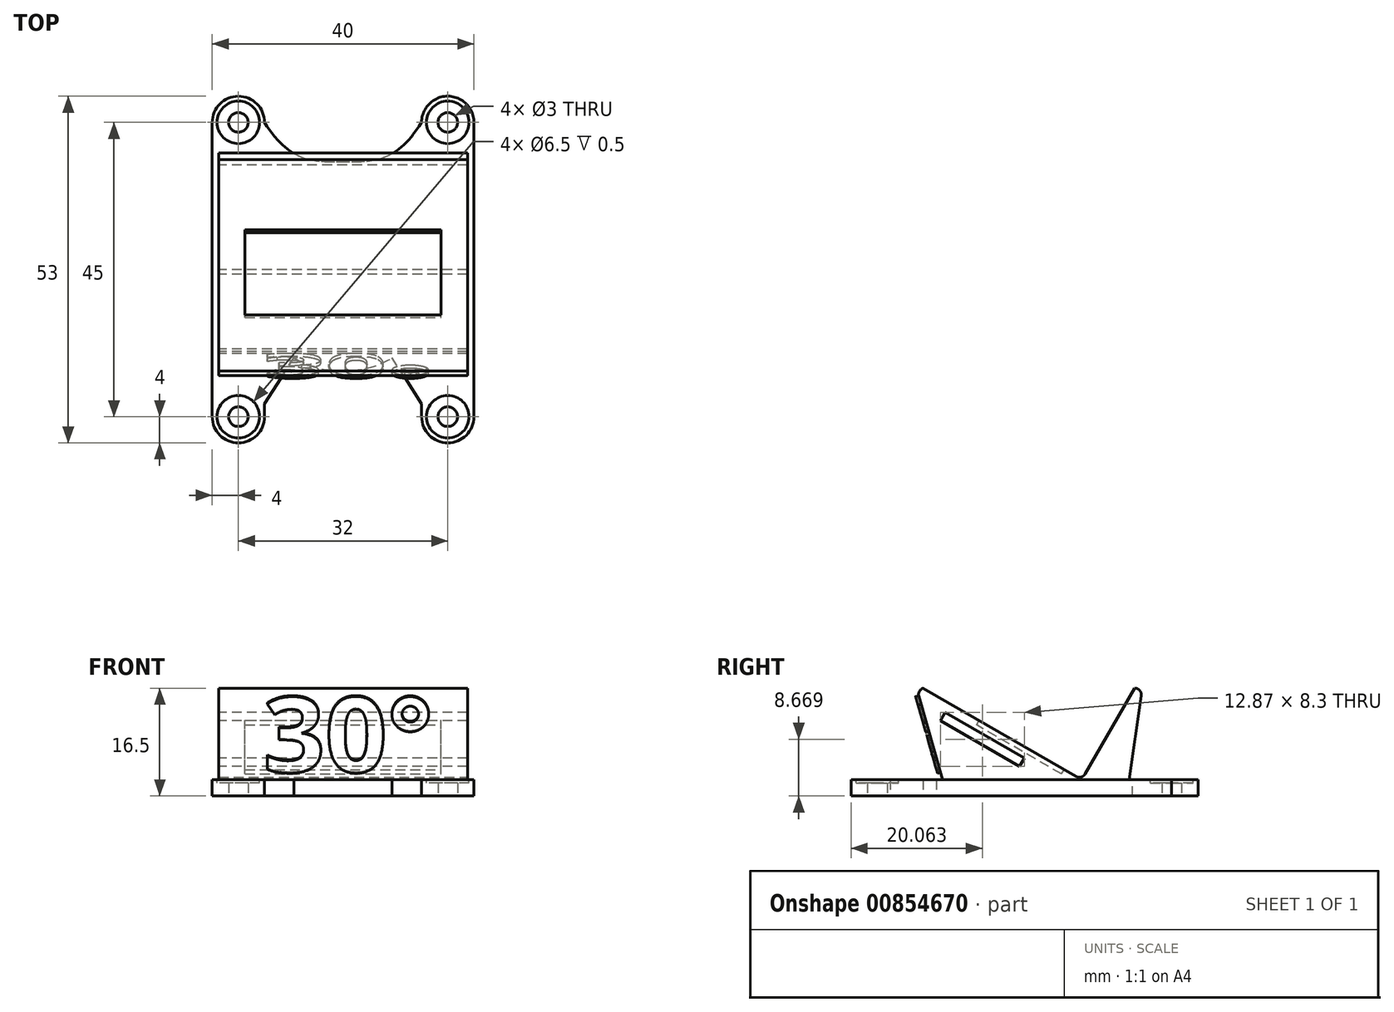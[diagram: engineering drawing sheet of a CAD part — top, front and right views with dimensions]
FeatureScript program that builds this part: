
annotation { "Feature Type Name" : "Feature", "Feature Type Description" : "" }
export const myFeature = defineFeature(function(context is Context, id is Id, definition is map)
    precondition{}
    {
        {
            var Q0;
            Q0=qCreatedBy(makeId("Top.planeOp"),FACE);
            var sketch = newSketch(context, id + "F0", { "sketchPlane" : qUnion([Q0])});
            skCircle(sketch, "E0", {"center": v(-16, 22.5) * mm, "radius": 4 * mm});
            skCircle(sketch, "E1", {"center": v(16, 22.5) * mm, "radius": 4 * mm});
            skCircle(sketch, "E2", {"center": v(-16, -22.5) * mm, "radius": 4 * mm});
            skCircle(sketch, "E3", {"center": v(16, -22.5) * mm, "radius": 4 * mm});
            skLineSegment(sketch, "E4", {"start": v(-20, 22.5) * mm, "end": v(-20, -22.5) * mm});
            skLineSegment(sketch, "E5", {"start": v(20, 22.55) * mm, "end": v(20, -22.5) * mm});
            skLineSegment(sketch, "E6", {"start": v(-12, -22.5) * mm, "end": v(-12, -20.5) * mm});
            skLineSegment(sketch, "E7", {"start": v(12, -22.5) * mm, "end": v(12, -20.5) * mm});
            skLineSegment(sketch, "E8", {"start": v(-12, -20.5) * mm, "end": v(-7.5, -13.5) * mm});
            skLineSegment(sketch, "E9", {"start": v(12, -20.5) * mm, "end": v(7.5, -13.5) * mm});
            skFitSpline(sketch, "E10", {"points": [v(-7.5, -13.5) * mm, v(0, -15.5) * mm, v(7.5, -13.5) * mm], "startDerivative": vector(15, -9) * mm, "endDerivative": vector(15, 9) * mm});
            skFitSpline(sketch, "E11", {"points": [v(-12, 22.5) * mm, v(0, 16.5) * mm, v(12, 22.5) * mm], "startDerivative": vector(24, -39) * mm, "endDerivative": vector(24, 39) * mm});
            skSolve(sketch);
        }
        {
            var Q0;
            Q0=qSketchRegion(id+"F0",true);
            extrude(context, id + "F1", {"entities" : qUnion([Q0]), "depth" : 2.5 * mm, "offsetDistance" : 25 * mm});
        }
        {
            var Q0;
            Q0=qCreatedBy(makeId("Right.planeOp"),FACE);
            var sketch = newSketch(context, id + "F2", { "sketchPlane" : qUnion([Q0])});
            skLineSegment(sketch, "E12", {"start": v(16, 2.5) * mm, "end": v(-12.5, 2.5) * mm});
            skLineSegment(sketch, "E13", {"start": v(-12.5, 2.5) * mm, "end": v(-16.5, 16.5) * mm});
            skLineSegment(sketch, "E14", {"start": v(-16.5, 16.5) * mm, "end": v(18, 16.5) * mm});
            skLineSegment(sketch, "E15", {"start": v(18, 16.5) * mm, "end": v(16, 2.5) * mm});
            skSolve(sketch);
        }
        {
            var Q0;
            Q0=qSketchRegion(id+"F2",true);
            extrude(context, id + "F3", {"entities" : qUnion([Q0]), "endBound" : BoundingType.SYMMETRIC, "depth" : 38 * mm, "offsetDistance" : 25 * mm});
        }
        {
            var Q0;
            Q0=makeQuery(id+"F3.opExtrude","CAP_FACE",FACE,{"disambiguationData":[OSD([sQuery(id+"F2.wireOp",EDGE,"YzHD2A4w-FKaB-bjk7-Ghrs-dXmW5guKQ4VY"),sQuery(id+"F2.wireOp",EDGE,"E12"),sQuery(id+"F2.wireOp",EDGE,"E13"),sQuery(id+"F2.wireOp",EDGE,"E14"),sQuery(id+"F2.wireOp",EDGE,"zXvGVPE5-xHOz-sBgs-eNty-2IJ9yV3vvyon")])],"isStart":true});
            var sketch = newSketch(context, id + "F4", { "sketchPlane" : qUnion([Q0])});
            skLineSegment(sketch, "E16", {"start": v(-16.83, 16.5) * mm, "end": v(-8.75, 2.5) * mm});
            skLineSegment(sketch, "E17", {"start": v(-8.75, 2.5) * mm, "end": v(15.5, 16.5) * mm});
            skLineSegment(sketch, "E18", {"start": v(15.5, 16.5) * mm, "end": v(-16.83, 16.5) * mm});
            skSolve(sketch);
        }
        {
            var Q0;
            Q0=qSketchRegion(id+"F4",true);
            extrude(context, id + "F5", {"entities" : qUnion([Q0]), "oppositeDirection" : true, "depth" : 40 * mm, "offsetDistance" : 25 * mm});
        }
        {
            var Q0;
            Q0=makeQuery(id+"F5.opExtrude","SWEPT_BODY",BODY,{"disambiguationData":[OSD([sQuery(id+"F4.wireOp",EDGE,"E16"),sQuery(id+"F4.wireOp",EDGE,"E17"),sQuery(id+"F4.wireOp",EDGE,"E18")])]});
            var Q1;
            Q1=makeQuery(id+"F3.opExtrude","SWEPT_BODY",BODY,{"disambiguationData":[OSD([sQuery(id+"F2.wireOp",EDGE,"YzHD2A4w-FKaB-bjk7-Ghrs-dXmW5guKQ4VY"),sQuery(id+"F2.wireOp",EDGE,"E12"),sQuery(id+"F2.wireOp",EDGE,"E13"),sQuery(id+"F2.wireOp",EDGE,"E14"),sQuery(id+"F2.wireOp",EDGE,"zXvGVPE5-xHOz-sBgs-eNty-2IJ9yV3vvyon")])]});
            booleanBodies(context, id + "F6", {"operationType" : BooleanOperationType.SUBTRACTION, "tools" : qUnion([Q0]), "targets" : qUnion([Q1])});
        }
        {
            var Q0;
            Q0=sQuery(id+"F0.wireOp",VERTEX,"E0.center");
            var Q1;
            Q1=sQuery(id+"F0.wireOp",VERTEX,"E1.center");
            var Q2;
            Q2=sQuery(id+"F0.wireOp",VERTEX,"E2.center");
            var Q3;
            Q3=sQuery(id+"F0.wireOp",VERTEX,"E3.center");
            var Q4;
            Q4=makeQuery(id+"F1.opExtrude","SWEPT_BODY",BODY,{"disambiguationData":[OSD([sQuery(id+"F0.wireOp",EDGE,"E0"),sQuery(id+"F0.wireOp",EDGE,"E1"),sQuery(id+"F0.wireOp",EDGE,"E2"),sQuery(id+"F0.wireOp",EDGE,"E3"),sQuery(id+"F0.wireOp",EDGE,"E4"),sQuery(id+"F0.wireOp",EDGE,"E5"),sQuery(id+"F0.wireOp",EDGE,"E6"),sQuery(id+"F0.wireOp",EDGE,"E7"),sQuery(id+"F0.wireOp",EDGE,"E8"),sQuery(id+"F0.wireOp",EDGE,"E9"),sQuery(id+"F0.wireOp",EDGE,"E10"),sQuery(id+"F0.wireOp",EDGE,"E11")])]});
            hole(context, id + "F7", {"style" : HoleStyle.SIMPLE, "endStyle" : HoleEndStyle.THROUGH, "oppositeDirection" : true, "holeDiameter" : 3 * mm, "tappedDepth" : 12 * mm, "tapClearance" : 3, "locations" : qUnion([Q0, Q1, Q2, Q3]), "scope" : qUnion([Q4])});
        }
        {
            var Q0;
            Q0=makeQuery(id+"F1.opExtrude","CAP_FACE",FACE,{"disambiguationData":[OSD([sQuery(id+"F0.wireOp",EDGE,"E0"),sQuery(id+"F0.wireOp",EDGE,"E1"),sQuery(id+"F0.wireOp",EDGE,"E2"),sQuery(id+"F0.wireOp",EDGE,"E3"),sQuery(id+"F0.wireOp",EDGE,"E4"),sQuery(id+"F0.wireOp",EDGE,"E5"),sQuery(id+"F0.wireOp",EDGE,"E6"),sQuery(id+"F0.wireOp",EDGE,"E7"),sQuery(id+"F0.wireOp",EDGE,"E8"),sQuery(id+"F0.wireOp",EDGE,"E9"),sQuery(id+"F0.wireOp",EDGE,"E10"),sQuery(id+"F0.wireOp",EDGE,"E11")])],"isStart":false});
            var sketch = newSketch(context, id + "F8", { "sketchPlane" : qUnion([Q0])});
            skCircle(sketch, "E19", {"center": v(-16, 22.5) * mm, "radius": 3.25 * mm});
            skCircle(sketch, "E20", {"center": v(16, 22.5) * mm, "radius": 3.25 * mm});
            skCircle(sketch, "E21", {"center": v(-16, -22.5) * mm, "radius": 3.25 * mm});
            skCircle(sketch, "E22", {"center": v(16, -22.5) * mm, "radius": 3.25 * mm});
            skSolve(sketch);
        }
        {
            var Q0;
            Q0=qSketchRegion(id+"F8",true);
            extrude(context, id + "F9", {"entities" : qUnion([Q0]), "oppositeDirection" : true, "depth" : 0.5 * mm, "offsetDistance" : 25 * mm});
        }
        {
            var Q0;
            Q0=makeQuery(id+"F9.opExtrude","SWEPT_BODY",BODY,{"disambiguationData":[OSD([sQuery(id+"F8.wireOp",EDGE,"E19")])]});
            var Q1;
            Q1=makeQuery(id+"F9.opExtrude","SWEPT_BODY",BODY,{"disambiguationData":[OSD([sQuery(id+"F8.wireOp",EDGE,"E20")])]});
            var Q2;
            Q2=makeQuery(id+"F9.opExtrude","SWEPT_BODY",BODY,{"disambiguationData":[OSD([sQuery(id+"F8.wireOp",EDGE,"E21")])]});
            var Q3;
            Q3=makeQuery(id+"F9.opExtrude","SWEPT_BODY",BODY,{"disambiguationData":[OSD([sQuery(id+"F8.wireOp",EDGE,"E22")])]});
            var Q4;
            Q4=makeQuery(id+"F1.opExtrude","SWEPT_BODY",BODY,{"disambiguationData":[OSD([sQuery(id+"F0.wireOp",EDGE,"E0"),sQuery(id+"F0.wireOp",EDGE,"E1"),sQuery(id+"F0.wireOp",EDGE,"E2"),sQuery(id+"F0.wireOp",EDGE,"E3"),sQuery(id+"F0.wireOp",EDGE,"E4"),sQuery(id+"F0.wireOp",EDGE,"E5"),sQuery(id+"F0.wireOp",EDGE,"E6"),sQuery(id+"F0.wireOp",EDGE,"E7"),sQuery(id+"F0.wireOp",EDGE,"E8"),sQuery(id+"F0.wireOp",EDGE,"E9"),sQuery(id+"F0.wireOp",EDGE,"E10"),sQuery(id+"F0.wireOp",EDGE,"E11")])]});
            booleanBodies(context, id + "F10", {"operationType" : BooleanOperationType.SUBTRACTION, "tools" : qUnion([Q0, Q1, Q2, Q3]), "targets" : qUnion([Q4])});
        }
        {
            var Q0;
            Q0=makeQuery(id+"F6.opBoolean","COPY",FACE,{"derivedFrom":makeQuery(id+"F5.opExtrude","SWEPT_FACE",FACE,{"disambiguationData":[OSD([sQuery(id+"F4.wireOp",EDGE,"E17")])]})});
            var sketch = newSketch(context, id + "F11", { "sketchPlane" : qUnion([Q0])});
            skLineSegment(sketch, "E23.bottom", {"start": v(-15, 3.22) * mm, "end": v(15, 3.22) * mm});
            skLineSegment(sketch, "E23.top", {"start": v(-15, -11.78) * mm, "end": v(15, -11.78) * mm});
            skLineSegment(sketch, "E23.left", {"start": v(-15, 3.22) * mm, "end": v(-15, -11.78) * mm});
            skLineSegment(sketch, "E23.right", {"start": v(15, 3.22) * mm, "end": v(15, -11.78) * mm});
            skSolve(sketch);
        }
        {
            var Q0;
            Q0=qSketchRegion(id+"F11",true);
            extrude(context, id + "F12", {"entities" : qUnion([Q0]), "oppositeDirection" : true, "depth" : 0.8 * mm, "offsetDistance" : 25 * mm});
        }
        {
            var Q0;
            Q0=makeQuery(id+"F12.opExtrude","SWEPT_BODY",BODY,{"disambiguationData":[OSD([sQuery(id+"F11.wireOp",EDGE,"E23.bottom"),sQuery(id+"F11.wireOp",EDGE,"E23.top"),sQuery(id+"F11.wireOp",EDGE,"E23.left"),sQuery(id+"F11.wireOp",EDGE,"E23.right")])]});
            var Q1;
            Q1=makeQuery(id+"F6.opBoolean","SPLIT",BODY,{"disambiguationData":[OD(1.0)],"derivedFrom":makeQuery(id+"F3.opExtrude","SWEPT_BODY",BODY,{"disambiguationData":[OSD([sQuery(id+"F2.wireOp",EDGE,"YzHD2A4w-FKaB-bjk7-Ghrs-dXmW5guKQ4VY"),sQuery(id+"F2.wireOp",EDGE,"E12"),sQuery(id+"F2.wireOp",EDGE,"E13"),sQuery(id+"F2.wireOp",EDGE,"E14"),sQuery(id+"F2.wireOp",EDGE,"zXvGVPE5-xHOz-sBgs-eNty-2IJ9yV3vvyon")])]})});
            var Q2;
            Q2=makeQuery(id+"F6.opBoolean","SPLIT",BODY,{"disambiguationData":[OD(0.0)],"derivedFrom":makeQuery(id+"F3.opExtrude","SWEPT_BODY",BODY,{"disambiguationData":[OSD([sQuery(id+"F2.wireOp",EDGE,"E12"),sQuery(id+"F2.wireOp",EDGE,"E13"),sQuery(id+"F2.wireOp",EDGE,"E14"),sQuery(id+"F2.wireOp",EDGE,"E15")])]})});
            booleanBodies(context, id + "F13", {"operationType" : BooleanOperationType.SUBTRACTION, "tools" : qUnion([Q0]), "targets" : qUnion([Q1, Q2])});
        }
        {
            var Q0;
            {var subQ0=sQuery(id+"F2.wireOp",EDGE,"E12");var subQ1=sQuery(id+"F2.wireOp",EDGE,"E13");Q0=makeQuery(id+"F6.opBoolean","SPLIT",FACE,{"disambiguationData":[TD([makeQuery(id+"F3.opExtrude","SWEPT_FACE",FACE,{"disambiguationData":[OSD([subQ1])]})])],"derivedFrom":makeQuery(id+"F3.opExtrude","CAP_FACE",FACE,{"disambiguationData":[OSD([sQuery(id+"F2.wireOp",EDGE,"YzHD2A4w-FKaB-bjk7-Ghrs-dXmW5guKQ4VY"),subQ0,subQ1,sQuery(id+"F2.wireOp",EDGE,"E14"),sQuery(id+"F2.wireOp",EDGE,"zXvGVPE5-xHOz-sBgs-eNty-2IJ9yV3vvyon")])],"isStart":true})});}
            var sketch = newSketch(context, id + "F14", { "sketchPlane" : qUnion([Q0])});
            skLineSegment(sketch, "E24", {"start": v(0, 5.82) * mm, "end": v(12.12, 12.82) * mm});
            skLineSegment(sketch, "E25", {"start": v(12.12, 12.82) * mm, "end": v(12.87, 11.52) * mm});
            skLineSegment(sketch, "E26", {"start": v(12.87, 11.52) * mm, "end": v(0.75, 4.52) * mm});
            skLineSegment(sketch, "E27", {"start": v(0.75, 4.52) * mm, "end": v(0, 5.82) * mm});
            skSolve(sketch);
        }
        {
            var Q0;
            Q0=qSketchRegion(id+"F14",true);
            extrude(context, id + "F15", {"entities" : qUnion([Q0]), "oppositeDirection" : true, "depth" : 40 * mm, "offsetDistance" : 25 * mm});
        }
        {
            var Q0;
            Q0=makeQuery(id+"F15.opExtrude","SWEPT_BODY",BODY,{"disambiguationData":[OSD([sQuery(id+"F14.wireOp",EDGE,"E24"),sQuery(id+"F14.wireOp",EDGE,"E25"),sQuery(id+"F14.wireOp",EDGE,"E26"),sQuery(id+"F14.wireOp",EDGE,"E27")])]});
            var Q1;
            Q1=makeQuery(id+"F6.opBoolean","SPLIT",BODY,{"disambiguationData":[OD(1.0)],"derivedFrom":makeQuery(id+"F3.opExtrude","SWEPT_BODY",BODY,{"disambiguationData":[OSD([sQuery(id+"F2.wireOp",EDGE,"YzHD2A4w-FKaB-bjk7-Ghrs-dXmW5guKQ4VY"),sQuery(id+"F2.wireOp",EDGE,"E12"),sQuery(id+"F2.wireOp",EDGE,"E13"),sQuery(id+"F2.wireOp",EDGE,"E14"),sQuery(id+"F2.wireOp",EDGE,"zXvGVPE5-xHOz-sBgs-eNty-2IJ9yV3vvyon")])]})});
            var Q2;
            Q2=makeQuery(id+"F6.opBoolean","SPLIT",BODY,{"disambiguationData":[OD(0.0)],"derivedFrom":makeQuery(id+"F3.opExtrude","SWEPT_BODY",BODY,{"disambiguationData":[OSD([sQuery(id+"F2.wireOp",EDGE,"E12"),sQuery(id+"F2.wireOp",EDGE,"E13"),sQuery(id+"F2.wireOp",EDGE,"E14"),sQuery(id+"F2.wireOp",EDGE,"E15")])]})});
            booleanBodies(context, id + "F16", {"operationType" : BooleanOperationType.SUBTRACTION, "tools" : qUnion([Q0]), "targets" : qUnion([Q1, Q2])});
        }
        {
            var Q0;
            Q0=makeQuery(id+"F1.opExtrude","SWEPT_BODY",BODY,{"disambiguationData":[OSD([sQuery(id+"F0.wireOp",EDGE,"E0"),sQuery(id+"F0.wireOp",EDGE,"E1"),sQuery(id+"F0.wireOp",EDGE,"E2"),sQuery(id+"F0.wireOp",EDGE,"E3"),sQuery(id+"F0.wireOp",EDGE,"E4"),sQuery(id+"F0.wireOp",EDGE,"E5"),sQuery(id+"F0.wireOp",EDGE,"E6"),sQuery(id+"F0.wireOp",EDGE,"E7"),sQuery(id+"F0.wireOp",EDGE,"E8"),sQuery(id+"F0.wireOp",EDGE,"E9"),sQuery(id+"F0.wireOp",EDGE,"E10"),sQuery(id+"F0.wireOp",EDGE,"E11")])]});
            var Q1;
            Q1=makeQuery(id+"F6.opBoolean","SPLIT",BODY,{"disambiguationData":[OD(0.0)],"derivedFrom":makeQuery(id+"F3.opExtrude","SWEPT_BODY",BODY,{"disambiguationData":[OSD([sQuery(id+"F2.wireOp",EDGE,"YzHD2A4w-FKaB-bjk7-Ghrs-dXmW5guKQ4VY"),sQuery(id+"F2.wireOp",EDGE,"E12"),sQuery(id+"F2.wireOp",EDGE,"E13"),sQuery(id+"F2.wireOp",EDGE,"E14"),sQuery(id+"F2.wireOp",EDGE,"zXvGVPE5-xHOz-sBgs-eNty-2IJ9yV3vvyon")])]})});
            var Q2;
            Q2=makeQuery(id+"F6.opBoolean","SPLIT",BODY,{"disambiguationData":[OD(1.0)],"derivedFrom":makeQuery(id+"F3.opExtrude","SWEPT_BODY",BODY,{"disambiguationData":[OSD([sQuery(id+"F2.wireOp",EDGE,"YzHD2A4w-FKaB-bjk7-Ghrs-dXmW5guKQ4VY"),sQuery(id+"F2.wireOp",EDGE,"E12"),sQuery(id+"F2.wireOp",EDGE,"E13"),sQuery(id+"F2.wireOp",EDGE,"E14"),sQuery(id+"F2.wireOp",EDGE,"zXvGVPE5-xHOz-sBgs-eNty-2IJ9yV3vvyon")])]})});
            booleanBodies(context, id + "F17", {"operationType" : BooleanOperationType.UNION, "tools" : qUnion([Q0, Q1, Q2])});
        }
        {
            var Q0;
            Q0=makeQuery(id+"F3.opExtrude","SWEPT_EDGE",EDGE,{"disambiguationData":[OSD([sQuery(id+"F2.wireOp",EDGE,"E12"),sQuery(id+"F2.wireOp",EDGE,"E13")])]});
            var Q1;
            Q1=makeQuery(id+"F3.opExtrude","SWEPT_EDGE",EDGE,{"disambiguationData":[OSD([sQuery(id+"F2.wireOp",EDGE,"E14"),sQuery(id+"F2.wireOp",EDGE,"zXvGVPE5-xHOz-sBgs-eNty-2IJ9yV3vvyon")])]});
            var Q2;
            {var subQ0=sQuery(id+"F2.wireOp",EDGE,"E12");var subQ2=sQuery(id+"F4.wireOp",EDGE,"E17");var subQ3=sQuery(id+"F4.wireOp",EDGE,"E16");var subQ4=makeQuery(id+"F5.opExtrude","SWEPT_EDGE",EDGE,{"disambiguationData":[OSD([subQ0,subQ3,subQ2])]});Q2=makeQuery(id+"F17.opBoolean","MERGE",EDGE,{"derivedFrom":[makeQuery(id+"F6.opBoolean","COPY",EDGE,{"disambiguationData":[topologyDisambiguationEdgeConnected([makeQuery(id+"F5.opExtrude","SWEPT_FACE",FACE,{"disambiguationData":[OSD([subQ3])]})])],"derivedFrom":subQ4}),makeQuery(id+"F6.opBoolean","COPY",EDGE,{"disambiguationData":[topologyDisambiguationEdgeConnected([makeQuery(id+"F5.opExtrude","SWEPT_FACE",FACE,{"disambiguationData":[OSD([subQ2])]})])],"derivedFrom":subQ4})]});}
            var Q3;
            Q3=makeQuery(id+"F3.opExtrude","SWEPT_EDGE",EDGE,{"disambiguationData":[OSD([sQuery(id+"F2.wireOp",EDGE,"YzHD2A4w-FKaB-bjk7-Ghrs-dXmW5guKQ4VY"),sQuery(id+"F2.wireOp",EDGE,"E12")])]});
            fillet(context, id + "F18", {"entities" : qUnion([Q0, Q1, Q2, Q3]), "radius" : 1 * mm, "tangentPropagation" : true, "allowEdgeOverflow" : false});
        }
        {
            var Q0;
            Q0=makeQuery(id+"F3.opExtrude","SWEPT_FACE",FACE,{"disambiguationData":[OSD([sQuery(id+"F2.wireOp",EDGE,"E13")])]});
            var sketch = newSketch(context, id + "F19", { "sketchPlane" : qUnion([Q0])});
            skText(sketch, "E28", { "text": "30°", "fontName": "OpenSans-Bold.ttf"});
            const initialGuessF19  = {"E28": [-0.01224, 0.00716, 1, 0, 0.01196]};
            skSetInitialGuess(sketch, initialGuessF19);
            skSolve(sketch);
        }
        {
            var Q0;
            Q0 = qSketchRegion(id + "F19", true);
            extrude(context, id + "F20", {"entities" : qUnion([Q0]), "operationType" : NewBodyOperationType.ADD, "depth" : 0.5 * mm, "offsetDistance" : 25 * mm});
        }
    });
